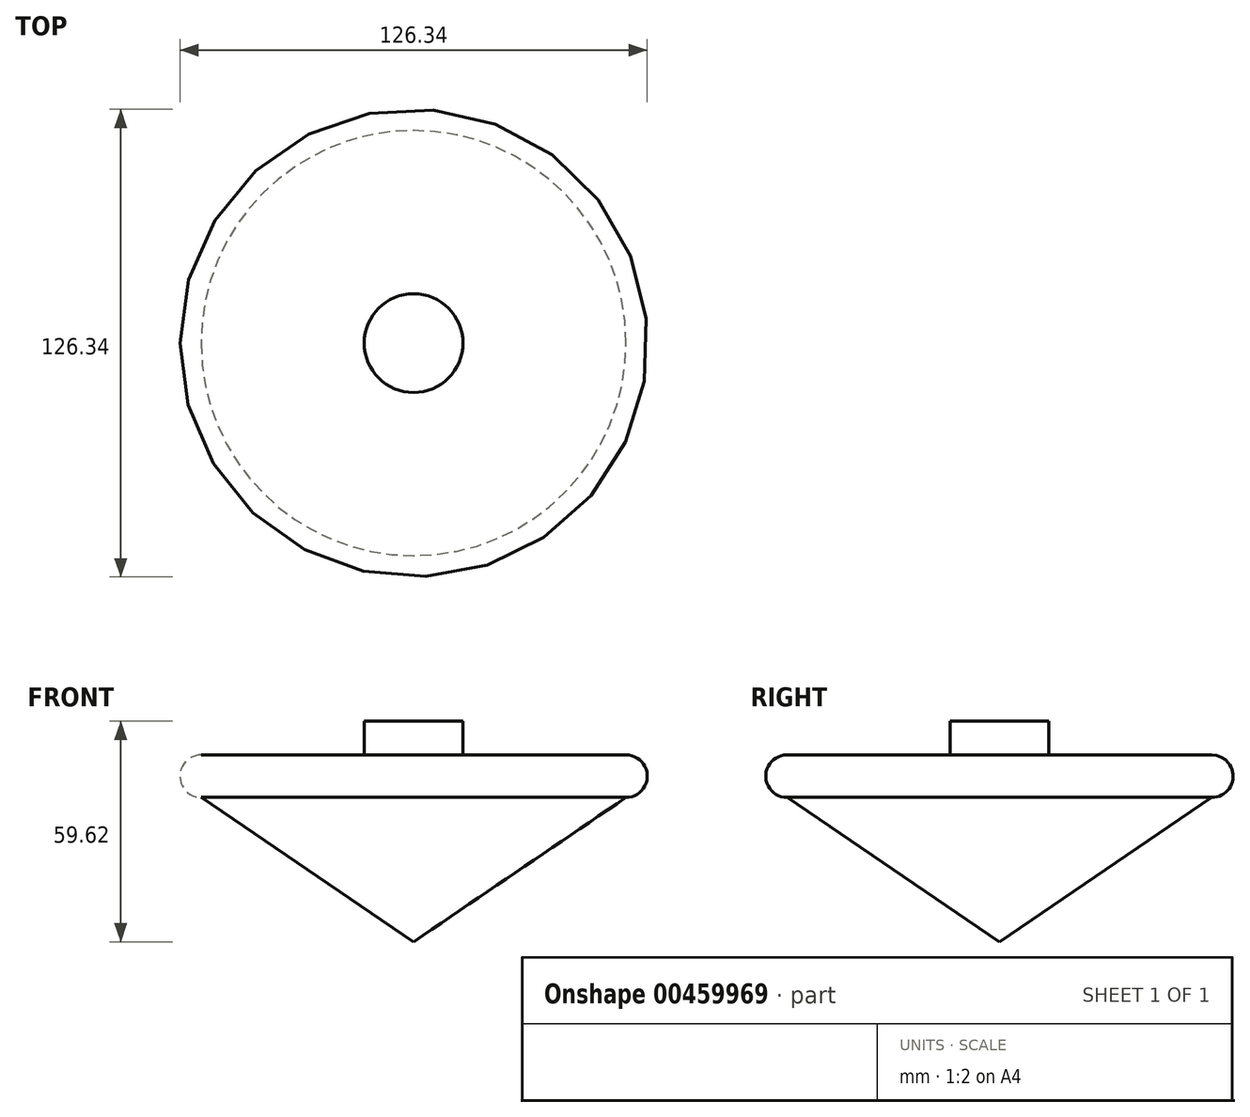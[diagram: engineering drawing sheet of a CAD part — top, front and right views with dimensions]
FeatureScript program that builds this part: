
annotation { "Feature Type Name" : "Feature", "Feature Type Description" : "" }
export const myFeature = defineFeature(function(context is Context, id is Id, definition is map)
    precondition{}
    {
        {
            var Q0;
            Q0=qCreatedBy(makeId("Front.planeOp"),FACE);
            var sketch = newSketch(context, id + "F0", { "sketchPlane" : qUnion([Q0])});
            skLineSegment(sketch, "E0", {"start": v(0, 5.7) * mm, "end": v(0, 65.32) * mm});
            skLineSegment(sketch, "E1", {"start": v(0, 56.2) * mm, "end": v(57.43, 56.2) * mm});
            skLineSegment(sketch, "E2", {"start": v(0, 44.72) * mm, "end": v(57.43, 44.72) * mm});
            skArc(sketch, "E3", {"start": v(57.43, 44.72) * mm, "mid": v(63.17, 50.46) * mm, "end": v(57.43, 56.2) * mm});
            skLineSegment(sketch, "E4", {"start": v(57.43, 44.72) * mm, "end": v(0, 5.7) * mm});
            skLineSegment(sketch, "E5", {"start": v(13.35, 56.2) * mm, "end": v(13.35, 65.32) * mm});
            skLineSegment(sketch, "E6", {"start": v(13.35, 65.32) * mm, "end": v(0, 65.32) * mm});
            skLineSegment(sketch, "E7", {"start": v(0, 5.7) * mm, "end": v(0, 0) * mm});
            skSolve(sketch);
        }
        {
            var Q0;
            Q0 = qSketchRegion(id + "F0", true);
            var Q1;
            Q1=sQuery(id+"F0.wireOp",EDGE,"E0");
            revolve(context, id + "F1", {"entities" : qUnion([Q0]), "axis" : qUnion([Q1]), "revolveType" : RevolveType.FULL});
        }
    });
